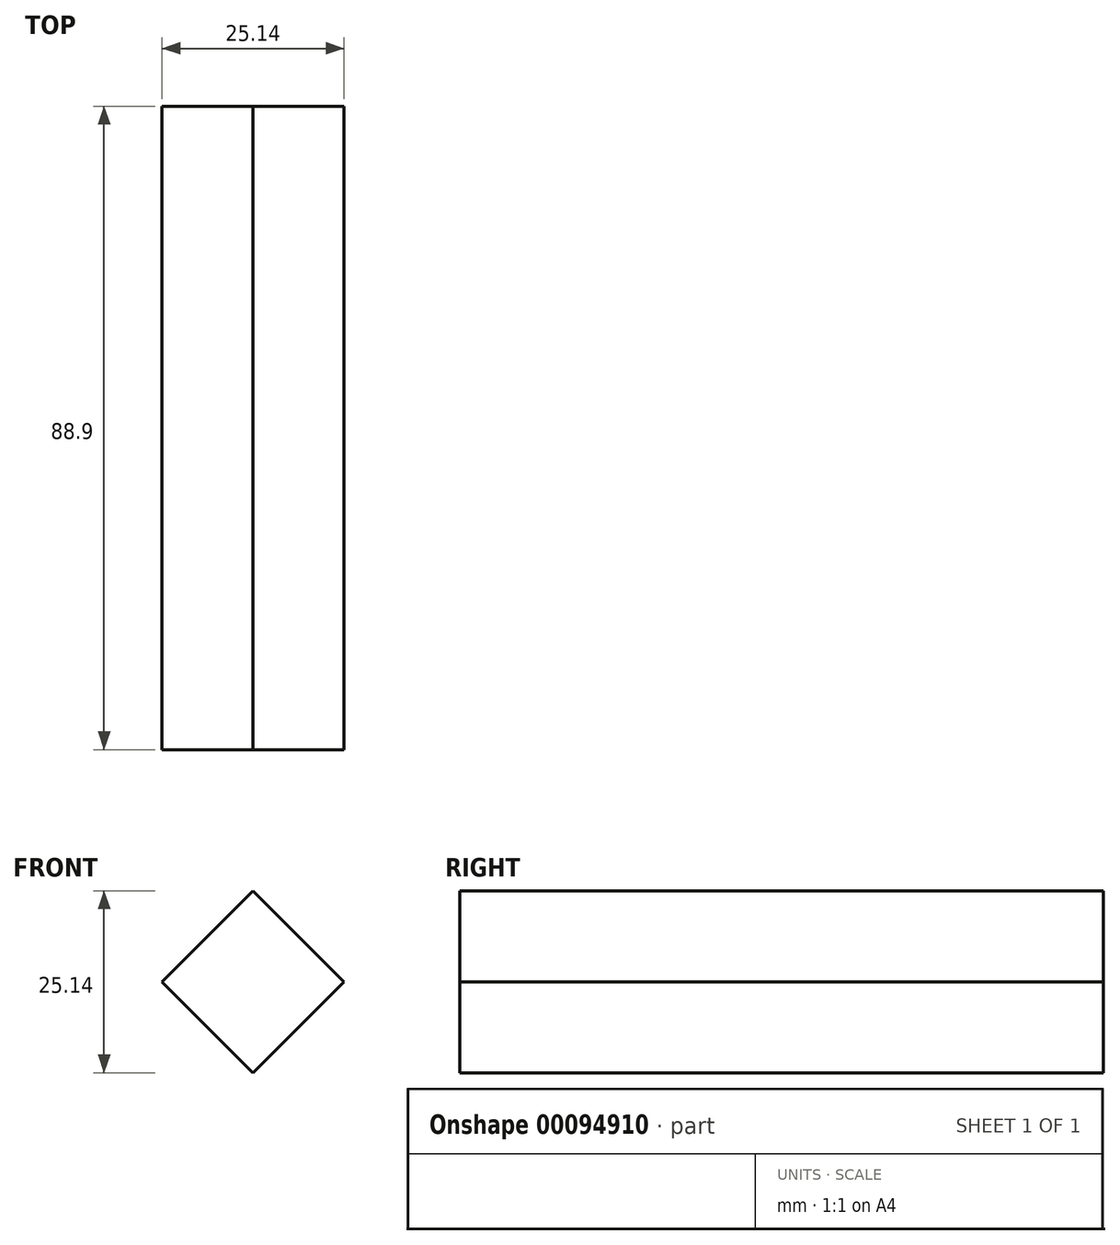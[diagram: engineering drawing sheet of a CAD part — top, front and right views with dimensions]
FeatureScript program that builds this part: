
annotation { "Feature Type Name" : "Feature", "Feature Type Description" : "" }
export const myFeature = defineFeature(function(context is Context, id is Id, definition is map)
    precondition{}
    {
        {
            var Q0;
            Q0=qCreatedBy(makeId("Front.planeOp"),FACE);
            var sketch = newSketch(context, id + "F0", { "sketchPlane" : qUnion([Q0])});
            skLineSegment(sketch, "E0", {"start": v(0, 0) * mm, "end": v(-12.57, -12.57) * mm});
            skLineSegment(sketch, "E1", {"start": v(-12.57, -12.57) * mm, "end": v(0, -25.14) * mm});
            skLineSegment(sketch, "E2", {"start": v(0, -25.14) * mm, "end": v(12.57, -12.57) * mm});
            skLineSegment(sketch, "E3", {"start": v(12.57, -12.57) * mm, "end": v(0, 0) * mm});
            skSolve(sketch);
        }
        {
            var Q0;
            Q0 = qSketchRegion(id + "F0", true);
            extrude(context, id + "F1", {"entities" : qUnion([Q0]), "depth" : 88.9 * mm});
        }
    });
